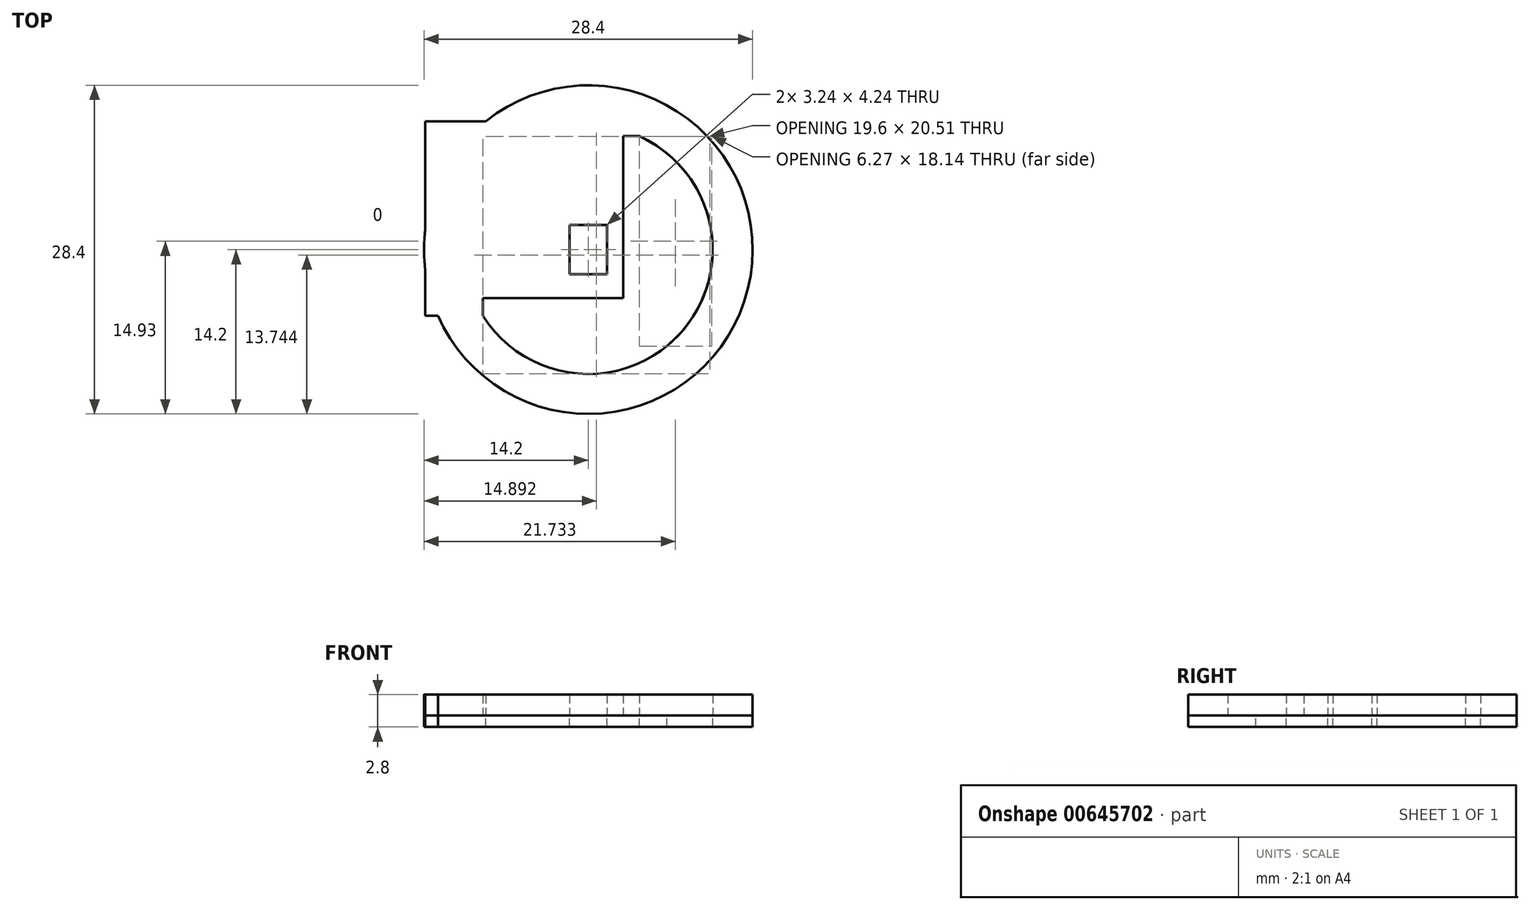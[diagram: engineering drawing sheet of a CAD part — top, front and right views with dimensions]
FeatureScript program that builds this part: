
annotation { "Feature Type Name" : "Feature", "Feature Type Description" : "" }
export const myFeature = defineFeature(function(context is Context, id is Id, definition is map)
    precondition{}
    {
        {
            var Q0;
            Q0=qCreatedBy(makeId("Top.planeOp"),FACE);
            var sketch = newSketch(context, id + "F0", { "sketchPlane" : qUnion([Q0])});
            skCircle(sketch, "E0", {"center": v(0, 0) * mm, "radius": 14.2 * mm});
            skLineSegment(sketch, "E1.bottom", {"start": v(-15.33, 15.34) * mm, "end": v(15.34, 15.34) * mm});
            skLineSegment(sketch, "E1.top", {"start": v(-15.34, -15.34) * mm, "end": v(15.33, -15.34) * mm});
            skLineSegment(sketch, "E1.left", {"start": v(-15.33, 15.34) * mm, "end": v(-15.34, -15.34) * mm});
            skLineSegment(sketch, "E1.right", {"start": v(15.34, 15.34) * mm, "end": v(15.33, -15.33) * mm});
            skLineSegment(sketch, "E2.bottom", {"start": v(-1.62, 2.12) * mm, "end": v(1.62, 2.12) * mm});
            skLineSegment(sketch, "E2.top", {"start": v(-1.62, -2.12) * mm, "end": v(1.62, -2.12) * mm});
            skLineSegment(sketch, "E2.left", {"start": v(-1.62, 2.12) * mm, "end": v(-1.62, -2.12) * mm});
            skLineSegment(sketch, "E2.right", {"start": v(1.62, 2.12) * mm, "end": v(1.62, -2.12) * mm});
            skLineSegment(sketch, "E3.bottom", {"start": v(-14.1, 5.7) * mm, "end": v(-13, 5.7) * mm});
            skLineSegment(sketch, "E3.left", {"start": v(-14.1, 5.7) * mm, "end": v(-14.1, -5.7) * mm});
            skLineSegment(sketch, "E3.right", {"start": v(4.4, 5.7) * mm, "end": v(4.4, -5.7) * mm});
            skArc(sketch, "E4", {"start": v(4.4, -9.8) * mm, "mid": v(10.75, 0) * mm, "end": v(4.4, 9.8) * mm});
            skLineSegment(sketch, "E5", {"start": v(4.4, 4.2) * mm, "end": v(4.4, -5.7) * mm});
            skLineSegment(sketch, "E6", {"start": v(3, -5.7) * mm, "end": v(3, 4.2) * mm});
            skLineSegment(sketch, "E7.trimOffspring", {"start": v(4.4, -11.1) * mm, "end": v(19.27, -11.1) * mm, "construction": true});
            skLineSegment(sketch, "E8.MirrorCS", {"start": v(-14.1, -5.7) * mm, "end": v(4.4, -5.7) * mm});
            skLineSegment(sketch, "E9.MirrorCS", {"start": v(-9.11, -4.2) * mm, "end": v(3, -4.2) * mm});
            skLineSegment(sketch, "E10.MirrorCS", {"start": v(-9.11, -5.7) * mm, "end": v(-9.11, -4.2) * mm});
            skArc(sketch, "E11.MirrorCS", {"start": v(4.4, 9.8) * mm, "mid": v(8.1, -7.06) * mm, "end": v(-9.11, -5.7) * mm});
            skLineSegment(sketch, "E12.MirrorCS", {"start": v(4.4, -4.2) * mm, "end": v(4.4, 9.8) * mm});
            skLineSegment(sketch, "E13.MirrorCS", {"start": v(4.4, -5.7) * mm, "end": v(4.4, 11.1) * mm});
            skLineSegment(sketch, "E14.MirrorCS", {"start": v(4.4, 11.1) * mm, "end": v(3, 11.1) * mm});
            skLineSegment(sketch, "E15.MirrorCS", {"start": v(-14.1, -5.7) * mm, "end": v(-14.1, 11.1) * mm});
            skLineSegment(sketch, "E16.MirrorCS", {"start": v(-14.1, 11.1) * mm, "end": v(3, 11.1) * mm});
            skLineSegment(sketch, "E17.MirrorCS", {"start": v(4.4, 9.8) * mm, "end": v(3, 9.8) * mm});
            skLineSegment(sketch, "E18.MirrorCS", {"start": v(3, 9.8) * mm, "end": v(3, -4.2) * mm});
            skPoint(sketch, "E19.orphan", {"position": v(-14.1, -11.1) * mm});
            skPoint(sketch, "E20.end.orphan", {"position": v(3, -11.1) * mm});
            skPoint(sketch, "E21.end.orphan", {"position": v(3, -9.8) * mm});
            skPoint(sketch, "E22.end.orphan", {"position": v(-9.11, 4.2) * mm});
            skPoint(sketch, "E23.orphan", {"position": v(-9.11, 5.7) * mm});
            skLineSegment(sketch, "E24.trimOffspring", {"start": v(3, 5.7) * mm, "end": v(4.4, 5.7) * mm});
            skSolve(sketch);
        }
        {
            var Q0;
            Q0 = qSketchRegion(id + "F0", true);
            var Q1;
            {var subQ0=sQuery(id+"F0.wireOp",EDGE,"E3.right");Q1=makeQuery(id+"F0.imprint","IMPRINT",FACE,{"disambiguationData":[TD([[makeQuery(id+"F0.imprint","IMPRINT",EDGE,{"derivedFrom":subQ0}),1.0]])]});}
            var Q2;
            {var subQ1=sQuery(id+"F0.wireOp",EDGE,"E3.right");Q2=makeQuery(id+"F0.imprint","IMPRINT",FACE,{"disambiguationData":[TD([[makeQuery(id+"F0.imprint","IMPRINT",EDGE,{"derivedFrom":subQ1}),-1.0]])]});}
            var Q3;
            {var subQ0=sQuery(id+"F0.wireOp",EDGE,"E13.MirrorCS");var subQ8=makeQuery(id+"F0.imprint","IMPRINT",VERTEX,{"disambiguationData":[OD(0.0)],"derivedFrom":subQ0});Q3=makeQuery(id+"F0.imprint","IMPRINT",FACE,{"disambiguationData":[TD([[makeQuery(id+"F0.imprint","IMPRINT",EDGE,{"disambiguationData":[TD([[subQ8,-1.0]])],"derivedFrom":subQ0}),-1.0]])]});}
            var Q4;
            {var subQ0=sQuery(id+"F0.wireOp",EDGE,"E6");Q4=makeQuery(id+"F0.imprint","IMPRINT",FACE,{"disambiguationData":[TD([[makeQuery(id+"F0.imprint","IMPRINT",EDGE,{"derivedFrom":subQ0}),1.0]])]});}
            var Q5;
            {var subQ4=sQuery(id+"F0.wireOp",EDGE,"E6");Q5=makeQuery(id+"F0.imprint","IMPRINT",FACE,{"disambiguationData":[TD([[makeQuery(id+"F0.imprint","IMPRINT",EDGE,{"derivedFrom":subQ4}),-1.0]])]});}
            var Q6;
            {var subQ0=sQuery(id+"F0.wireOp",EDGE,"E17.MirrorCS");Q6=makeQuery(id+"F0.imprint","IMPRINT",FACE,{"disambiguationData":[TD([[makeQuery(id+"F0.imprint","IMPRINT",EDGE,{"derivedFrom":subQ0}),1.0]])]});}
            var Q7;
            {var subQ0=sQuery(id+"F0.wireOp",EDGE,"E15.MirrorCS");var subQ1=sQuery(id+"F0.wireOp",EDGE,"E0");var subQ2=makeQuery(id+"F0.imprint","INTERSECT",VERTEX,{"disambiguationData":[OD(0.0)],"derivedFrom":[subQ1,subQ0]});Q7=makeQuery(id+"F0.imprint","IMPRINT",FACE,{"disambiguationData":[TD([[makeQuery(id+"F0.imprint","IMPRINT",EDGE,{"disambiguationData":[TD([[subQ2,-1.0]])],"derivedFrom":subQ1}),1.0]])]});}
            extrude(context, id + "F1", {"entities" : qUnion([Q0, Q1, Q2, Q3, Q4, Q5, Q6, Q7]), "oppositeDirection" : true, "depth" : 1 * mm, "offsetDistance" : 25 * mm});
        }
        {
            var Q0;
            Q0 = qSketchRegion(id + "F0", true);
            var Q1;
            {var subQ0=sQuery(id+"F0.wireOp",EDGE,"E0");var subQ1=makeQuery(id+"F0.imprint","INTERSECT",VERTEX,{"derivedFrom":[subQ0,sQuery(id+"F0.wireOp",EDGE,"JeHYszuU-w9v3-eTuM-VYGQ-MpFcW94nDwu7")]});Q1=makeQuery(id+"F0.imprint","IMPRINT",FACE,{"disambiguationData":[TD([[makeQuery(id+"F0.imprint","IMPRINT",EDGE,{"disambiguationData":[TD([[subQ1,1.0]])],"derivedFrom":subQ0}),-1.0]])]});}
            var Q2;
            {var subQ3=sQuery(id+"F0.wireOp",EDGE,"E4");Q2=makeQuery(id+"F0.imprint","IMPRINT",FACE,{"disambiguationData":[TD([[makeQuery(id+"F0.imprint","IMPRINT",EDGE,{"derivedFrom":subQ3}),-1.0]])]});}
            var Q3;
            {var subQ3=sQuery(id+"F0.wireOp",EDGE,"E4");Q3=makeQuery(id+"F0.imprint","IMPRINT",FACE,{"disambiguationData":[TD([[makeQuery(id+"F0.imprint","IMPRINT",EDGE,{"derivedFrom":subQ3}),1.0]])]});}
            var Q4;
            {var subQ0=sQuery(id+"F0.wireOp",EDGE,"E3.left");var subQ1=sQuery(id+"F0.wireOp",EDGE,"E0");var subQ2=makeQuery(id+"F0.imprint","INTERSECT",VERTEX,{"disambiguationData":[OD(0.0)],"derivedFrom":[subQ1,subQ0]});Q4=makeQuery(id+"F0.imprint","IMPRINT",FACE,{"disambiguationData":[TD([[makeQuery(id+"F0.imprint","IMPRINT",EDGE,{"disambiguationData":[TD([[subQ2,-1.0]])],"derivedFrom":subQ1}),1.0]])]});}
            var Q5;
            {var subQ8=sQuery(id+"F0.wireOp",EDGE,"E14.MirrorCS");Q5=makeQuery(id+"F0.imprint","IMPRINT",FACE,{"disambiguationData":[TD([[makeQuery(id+"F0.imprint","IMPRINT",EDGE,{"derivedFrom":subQ8}),-1.0]])]});}
            var Q6;
            {var subQ0=sQuery(id+"F0.wireOp",EDGE,"E13.MirrorCS");var subQ8=makeQuery(id+"F0.imprint","IMPRINT",VERTEX,{"disambiguationData":[OD(0.0)],"derivedFrom":subQ0});Q6=makeQuery(id+"F0.imprint","IMPRINT",FACE,{"disambiguationData":[TD([[makeQuery(id+"F0.imprint","IMPRINT",EDGE,{"disambiguationData":[TD([[subQ8,-1.0]])],"derivedFrom":subQ0}),-1.0]])]});}
            var Q7;
            {var subQ0=sQuery(id+"F0.wireOp",EDGE,"E15.MirrorCS");var subQ1=sQuery(id+"F0.wireOp",EDGE,"E0");var subQ2=makeQuery(id+"F0.imprint","INTERSECT",VERTEX,{"disambiguationData":[OD(0.0)],"derivedFrom":[subQ1,subQ0]});Q7=makeQuery(id+"F0.imprint","IMPRINT",FACE,{"disambiguationData":[TD([[makeQuery(id+"F0.imprint","IMPRINT",EDGE,{"disambiguationData":[TD([[subQ2,-1.0]])],"derivedFrom":subQ1}),1.0]])]});}
            extrude(context, id + "F2", {"entities" : qUnion([Q0, Q1, Q2, Q3, Q4, Q5, Q6, Q7]), "operationType" : NewBodyOperationType.ADD, "depth" : 1.8 * mm, "offsetDistance" : 25 * mm});
        }
    });
